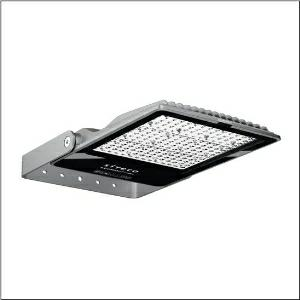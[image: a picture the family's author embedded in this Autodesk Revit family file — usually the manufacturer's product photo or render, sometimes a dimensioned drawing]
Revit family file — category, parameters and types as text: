
# Revit family: sicompact_r__31_midi___pl32_5xa7581d1k23_6975
name_source: partatom
category: Lighting Fixtures
units: mm (PartAtom-declared; Revit-internal decimal feet)

## family parameters
Cut with Voids When Loaded = No
Host = Face
Light Source = No
Part Type = Normal
Room Calculation Point = No
Round Connector Dimension = Use Diameter
Shared = No

## types (1)
- SiCompact® 31 midi  PL32 (1 x LED, 27000 lm, 171 W, 3000K)
    Apparent Load = 171 VA
    CIE Flux Codes = 32 69 98 100 100
    Color Rendering = 70
    Color Temperature = 3000K
    Default Elevation = 1800 mm
    Description = SiCompact® 31 midi, floodlight, primary light control with lens, of plastic, of toughened safety glass, transparent, light distribution: PL32, light emission: direct distribution, primary light characteristic: asymmetric, installation type: surface-mounted, LED, High Power LED, rated luminous flux: 27.000lm, luminous efficacy: 158lm/W, light colour: 730, colour temperature: 3000K, control gear: ON/OFF, with cable, 3x 1.5mm², mains connection: 220..240V, AC, 50/60Hz, connection cable pre-assembled, cable length: 2m, rated input power: 171W, of diecast aluminium, specular, metallic grey (RAL 9006), length: 560mm, width: 330mm, height: 62mm, bracket, of sheet steel, coated, metallic grey (RAL 9006), ON/OFF, protection rating (complete): IP66, insulation class (complete): insulation class I (protective earthing), certification: CE, ENEC, impact resistance: IK08, permissible operating ambient temperature: -40..+45°C, packaging unit: 1 piece

Light Distribution: PL32
    Height = 62 mm  [stored 0.203412 ft]
    Lamp = 1 x LED
    Lamp Light Flux = 27000 lm
    Lamp Power = 171 W
    Lamp count = 1
    Length = 560 mm
    Luminous efficacy = 158 lm/W
    Manufacturer = Siteco
    ModVariant = No
    Model = 5XA7581D1K23
    Mounting Place = Wall
    Mounting Type = Surface mounted
    Number of Poles = 1
    OnlyDefault = Yes
    Power Factor = 1
    Product Name = SiCompact® 31 midi | PL32
    Product group = floodlight | wall mounted
    ProductGroupID = 2001
    Protection Class = Protection class I
    Protection Degree = IP 66
    RLX_Detail_Level = 1
    RLX_Emergency_Light_Flux = 0 lm
    RLX_Emergency_Type = 0
    RLX_Emergency_Type_DB = No
    RlxData = <blob elided: 98321 chars, md5=e5c63364>
    Socket = socket
    Standby Power = 0 W
    System Light Flux = 27000 lm
    System Power = 171 W
    Type Comments = Product without accessories
    Type Image = l_1006415.jpg
    URL = http://relux.com
    VarID = ---
    Voltage = 0 V
    Weight = 0.00 kg
    Width = 333 mm

note: [stored X ft] marks values corroborated as IEEE doubles in the binary element streams (Revit-internal decimal feet)

## geometry (parser evidence)
native form markers: Blend x4, Sweep x12
no freeform markers — native parametric forms only
